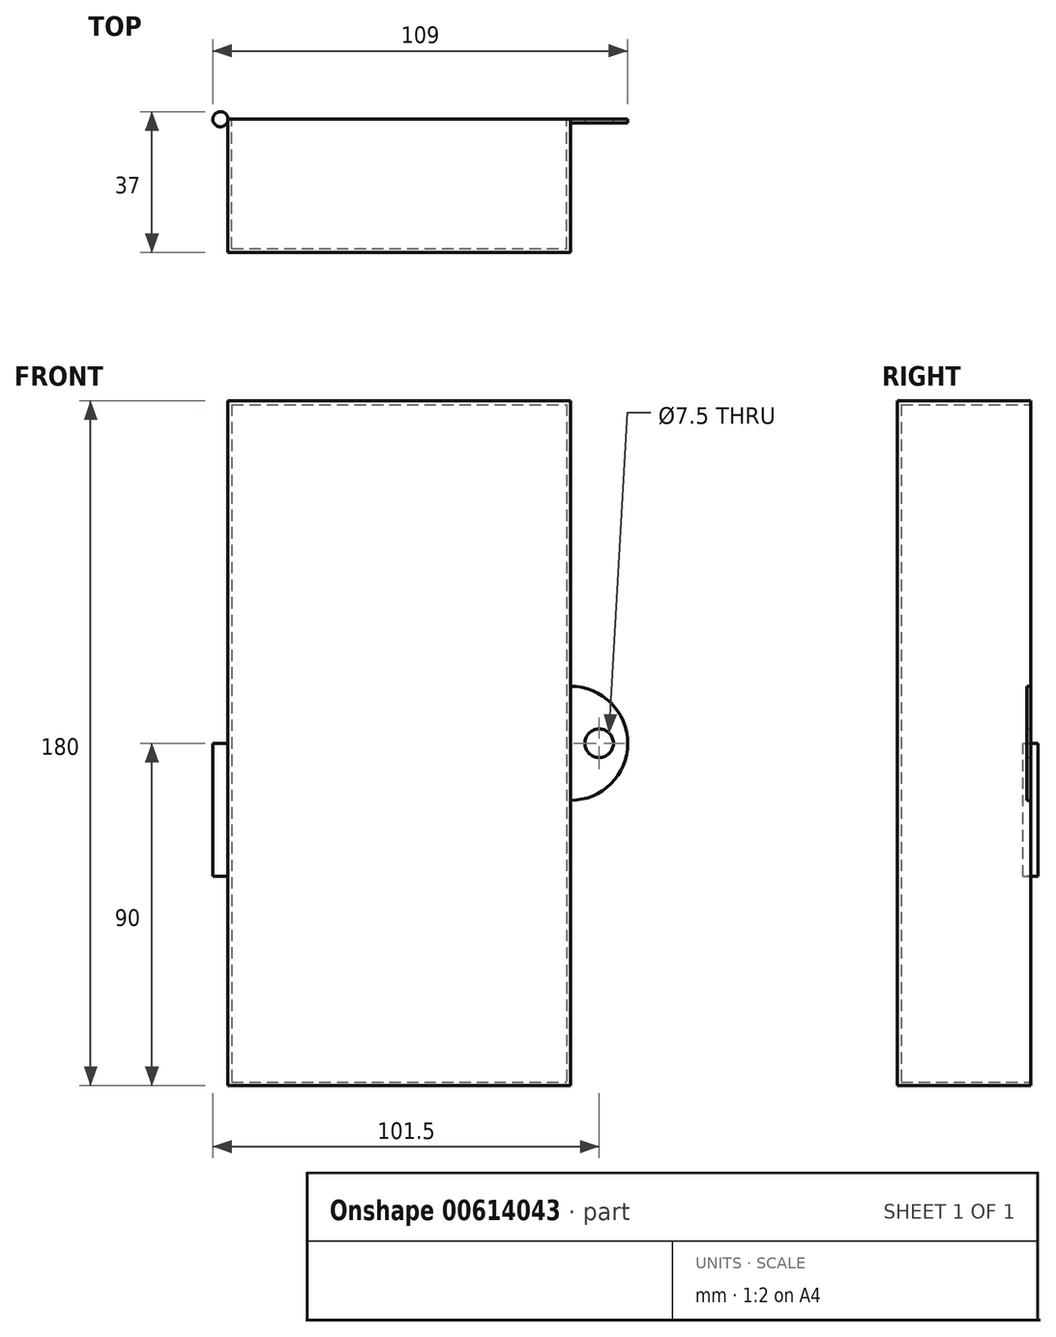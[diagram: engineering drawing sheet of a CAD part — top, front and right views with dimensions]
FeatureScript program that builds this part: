
annotation { "Feature Type Name" : "Feature", "Feature Type Description" : "" }
export const myFeature = defineFeature(function(context is Context, id is Id, definition is map)
    precondition{}
    {
        {
            var Q0;
            Q0=qCreatedBy(makeId("Front.planeOp"),FACE);
            var sketch = newSketch(context, id + "F0", { "sketchPlane" : qUnion([Q0])});
            skLineSegment(sketch, "E0.bottom", {"start": v(-45, 90) * mm, "end": v(45, 90) * mm});
            skLineSegment(sketch, "E0.top", {"start": v(-45, -90) * mm, "end": v(45, -90) * mm});
            skLineSegment(sketch, "E0.left", {"start": v(-45, 90) * mm, "end": v(-45, -90) * mm});
            skLineSegment(sketch, "E0.right", {"start": v(45, 90) * mm, "end": v(45, -90) * mm});
            skSolve(sketch);
        }
        {
            var Q0;
            Q0 = qSketchRegion(id + "F0", true);
            extrude(context, id + "F1", {"entities" : qUnion([Q0]), "depth" : 35 * mm, "offsetDistance" : 25 * mm});
        }
        {
            var Q0;
            Q0=makeQuery(id+"F1.opExtrude","CAP_FACE",FACE,{"disambiguationData":[OSD([sQuery(id+"F0.wireOp",EDGE,"E0.bottom"),sQuery(id+"F0.wireOp",EDGE,"E0.top"),sQuery(id+"F0.wireOp",EDGE,"E0.left"),sQuery(id+"F0.wireOp",EDGE,"E0.right")])],"isStart":true});
            shell(context, id + "F2", {"entities" : qUnion([Q0]), "thickness" : 1 * mm});
        }
        {
            var Q0;
            Q0=qCreatedBy(makeId("Front.planeOp"),FACE);
            var sketch = newSketch(context, id + "F3", { "sketchPlane" : qUnion([Q0])});
            skLineSegment(sketch, "E1", {"start": v(45, -43.69) * mm, "end": v(45, 54.69) * mm, "construction": true});
            skArc(sketch, "E2", {"start": v(45, 15) * mm, "mid": v(60, 0) * mm, "end": v(45, -15) * mm});
            skLineSegment(sketch, "E3", {"start": v(45, -15) * mm, "end": v(45, 15) * mm});
            skCircle(sketch, "E4", {"center": v(52.5, 0) * mm, "radius": 3.75 * mm});
            skSolve(sketch);
        }
        {
            var Q0;
            Q0 = qSketchRegion(id + "F3", true);
            extrude(context, id + "F4", {"entities" : qUnion([Q0]), "operationType" : NewBodyOperationType.ADD, "depth" : 1 * mm, "offsetDistance" : 25 * mm});
        }
        {
            var Q0;
            Q0=qCreatedBy(makeId("Top.planeOp"),FACE);
            var sketch = newSketch(context, id + "F5", { "sketchPlane" : qUnion([Q0])});
            skCircle(sketch, "E5", {"center": v(-47, 0) * mm, "radius": 2 * mm});
            skSolve(sketch);
        }
        {
            var Q0;
            Q0 = qSketchRegion(id + "F5", true);
            extrude(context, id + "F6", {"entities" : qUnion([Q0]), "operationType" : NewBodyOperationType.ADD, "oppositeDirection" : true, "depth" : 35 * mm, "offsetDistance" : 25 * mm});
        }
    });
